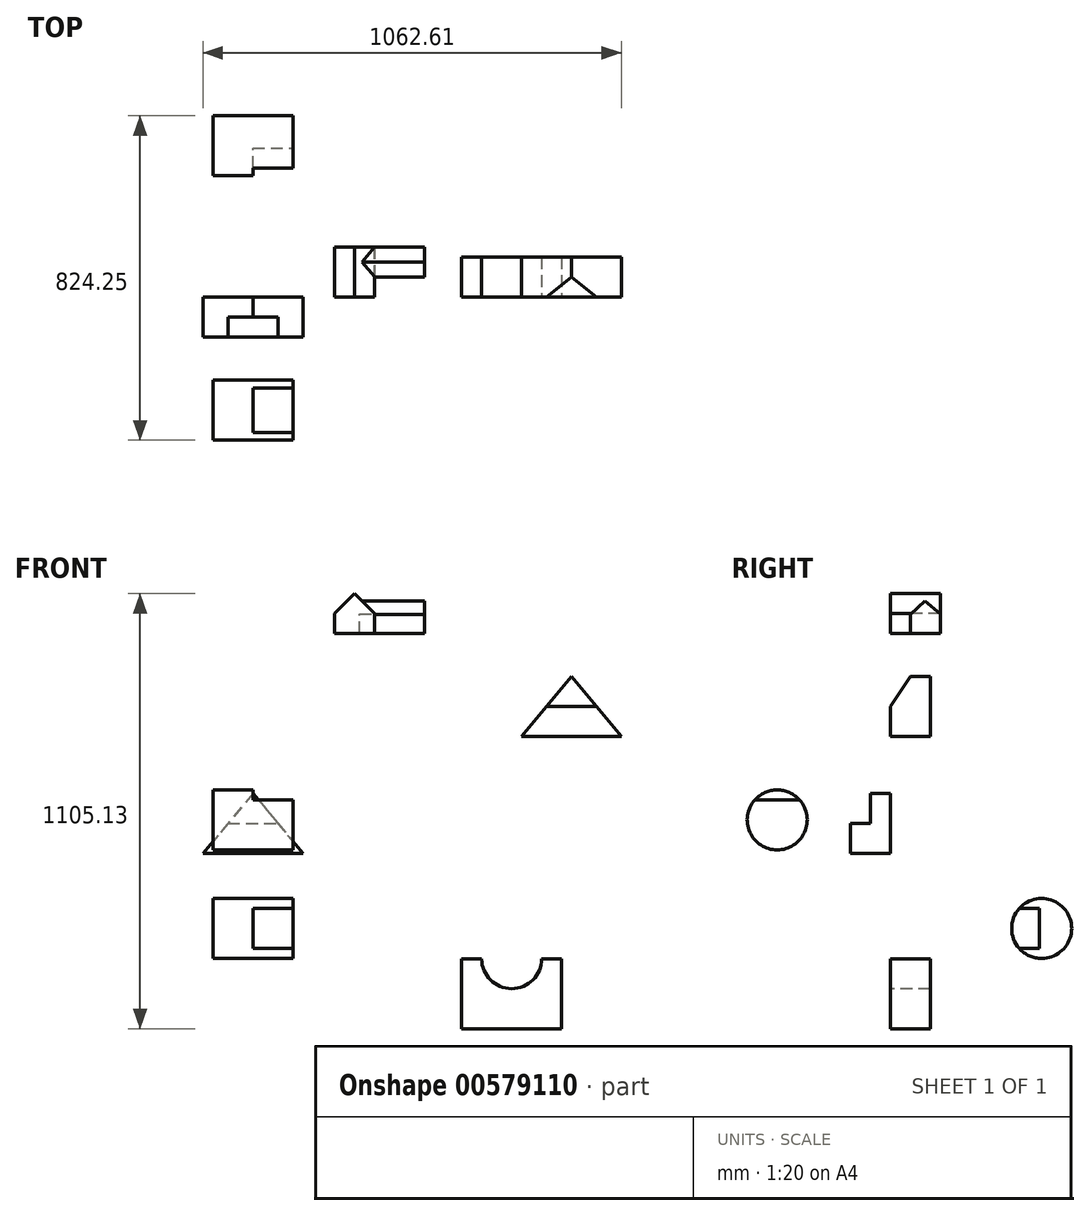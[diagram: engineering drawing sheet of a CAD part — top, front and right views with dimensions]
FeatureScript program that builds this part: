
annotation { "Feature Type Name" : "Feature", "Feature Type Description" : "" }
export const myFeature = defineFeature(function(context is Context, id is Id, definition is map)
    precondition{}
    {
        {
            var Q0;
            Q0=qCreatedBy(makeId("Front.planeOp"),FACE);
            var sketch = newSketch(context, id + "F0", { "sketchPlane" : qUnion([Q0])});
            skLineSegment(sketch, "E0", {"start": v(-228.36, -85.16) * mm, "end": v(25.64, -85.16) * mm});
            skLineSegment(sketch, "E1", {"start": v(-101.36, 67.24) * mm, "end": v(-37.86, -8.96) * mm});
            skLineSegment(sketch, "E2", {"start": v(-101.36, 67.24) * mm, "end": v(-164.86, -8.96) * mm});
            skLineSegment(sketch, "E3", {"start": v(-164.86, -8.96) * mm, "end": v(-37.86, -8.96) * mm});
            skLineSegment(sketch, "E4", {"start": v(-164.86, -8.96) * mm, "end": v(-228.36, -85.16) * mm});
            skLineSegment(sketch, "E5", {"start": v(-37.86, -8.96) * mm, "end": v(25.64, -85.16) * mm});
            skPoint(sketch, "E6.orphan", {"position": v(25.64, 67.24) * mm});
            skPoint(sketch, "E7.end.orphan", {"position": v(25.64, -8.96) * mm});
            skPoint(sketch, "E8.end.orphan", {"position": v(-228.36, -8.96) * mm});
            skPoint(sketch, "E9.end.orphan", {"position": v(-228.36, 67.24) * mm});
            skSolve(sketch);
        }
        {
            var Q0;
            Q0=makeQuery(id+"F0.imprint","IMPRINT",FACE,{"disambiguationData":[TD([[makeQuery(id+"F0.imprint","IMPRINT",EDGE,{"derivedFrom":sQuery(id+"F0.wireOp",EDGE,"E0")}),1.0]])]});
            extrude(context, id + "F1", {"entities" : qUnion([Q0]), "depth" : 101.6 * mm, "offsetDistance" : 25.4 * mm});
        }
        {
            var Q0;
            Q0 = qSketchRegion(id + "F0", true);
            extrude(context, id + "F2", {"entities" : qUnion([Q0]), "operationType" : NewBodyOperationType.ADD, "depth" : 50.8 * mm, "offsetDistance" : 25.4 * mm});
        }
        {
            var Q0;
            Q0=qCreatedBy(makeId("Front.planeOp"),FACE);
            var sketch = newSketch(context, id + "F3", { "sketchPlane" : qUnion([Q0])});
            skLineSegment(sketch, "E10", {"start": v(580.25, 364.98) * mm, "end": v(580.25, 212.58) * mm});
            skLineSegment(sketch, "E11", {"start": v(580.25, 212.58) * mm, "end": v(834.25, 212.58) * mm});
            skLineSegment(sketch, "E12", {"start": v(834.25, 212.58) * mm, "end": v(834.25, 364.98) * mm});
            skLineSegment(sketch, "E13", {"start": v(834.25, 364.98) * mm, "end": v(580.25, 364.98) * mm});
            skLineSegment(sketch, "E14", {"start": v(707.25, 364.98) * mm, "end": v(580.25, 212.58) * mm});
            skLineSegment(sketch, "E15", {"start": v(707.25, 364.98) * mm, "end": v(834.25, 212.58) * mm});
            skSolve(sketch);
        }
        {
            var Q0;
            Q0=makeQuery(id+"F3.imprint","IMPRINT",FACE,{"disambiguationData":[TD([[makeQuery(id+"F3.imprint","IMPRINT",EDGE,{"derivedFrom":sQuery(id+"F3.wireOp",EDGE,"E11")}),1.0]])]});
            extrude(context, id + "F4", {"entities" : qUnion([Q0]), "oppositeDirection" : true, "depth" : 101.6 * mm, "offsetDistance" : 25.4 * mm});
        }
        {
            var Q0;
            Q0=makeQuery(id+"F4.opExtrude","CAP_EDGE",EDGE,{"disambiguationData":[OSD([sQuery(id+"F3.wireOp",EDGE,"E11")])],"isStart":true});
            cPoint(context, id + "F5", {"entities" : qUnion([Q0]), "parameter" : 0.5});
        }
        {
            var Q0;
            Q0=makeQuery(id+"F4.opExtrude","CAP_VERTEX",VERTEX,{"disambiguationData":[OSD([sQuery(id+"F3.wireOp",EDGE,"E13"),sQuery(id+"F3.wireOp",EDGE,"E14"),sQuery(id+"F3.wireOp",EDGE,"E15")])],"isStart":true});
            var Q1;
            Q1=makeQuery(id+"F4.opExtrude","CAP_VERTEX",VERTEX,{"disambiguationData":[OSD([sQuery(id+"F3.wireOp",EDGE,"E13"),sQuery(id+"F3.wireOp",EDGE,"E14"),sQuery(id+"F3.wireOp",EDGE,"E15")])],"isStart":false});
            var Q2;
            Q2 = qCreatedBy(id + "F5" ,VERTEX);
            cPlane(context, id + "F6", {"entities" : qUnion([Q0, Q1, Q2]), "cplaneType" : CPlaneType.THREE_POINT, "offset" : 25.4 * mm, "width" : 152.4 * mm, "height" : 152.4 * mm});
        }
        {
            var Q0;
            Q0=qCreatedBy(id+"F6.planeOp",FACE);
            var sketch = newSketch(context, id + "F7", { "sketchPlane" : qUnion([Q0])});
            skLineSegment(sketch, "E16", {"start": v(0, 288.78) * mm, "end": v(50.8, 364.98) * mm});
            skLineSegment(sketch, "E17", {"start": v(50.8, 364.98) * mm, "end": v(0, 364.98) * mm});
            skLineSegment(sketch, "E18", {"start": v(0, 364.98) * mm, "end": v(0, 288.78) * mm});
            skSolve(sketch);
        }
        {
            var Q0;
            Q0 = qSketchRegion(id + "F7", true);
            extrude(context, id + "F8", {"entities" : qUnion([Q0]), "operationType" : NewBodyOperationType.REMOVE, "endBound" : BoundingType.SYMMETRIC, "oppositeDirection" : true, "depth" : 127 * mm, "offsetDistance" : 25.4 * mm});
        }
        {
            var Q0;
            Q0=qCreatedBy(makeId("Front.planeOp"),FACE);
            var sketch = newSketch(context, id + "F9", { "sketchPlane" : qUnion([Q0])});
            skLineSegment(sketch, "E19", {"start": v(106.32, 473.23) * mm, "end": v(207.92, 473.23) * mm});
            skLineSegment(sketch, "E20", {"start": v(207.92, 473.23) * mm, "end": v(207.92, 524.03) * mm});
            skLineSegment(sketch, "E21", {"start": v(207.92, 524.03) * mm, "end": v(157.12, 574.83) * mm});
            skPoint(sketch, "E21.endSnap0", {"position": v(157.12, 473.23) * mm});
            skLineSegment(sketch, "E22", {"start": v(106.32, 473.23) * mm, "end": v(106.32, 524.03) * mm});
            skLineSegment(sketch, "E23", {"start": v(106.32, 524.03) * mm, "end": v(157.12, 574.83) * mm});
            skLineSegment(sketch, "E24", {"start": v(207.92, 524.03) * mm, "end": v(334.92, 524.03) * mm});
            skLineSegment(sketch, "E25", {"start": v(334.92, 524.03) * mm, "end": v(334.92, 473.23) * mm});
            skLineSegment(sketch, "E26", {"start": v(334.92, 473.23) * mm, "end": v(207.92, 473.23) * mm});
            skSolve(sketch);
        }
        {
            var Q0;
            Q0=makeQuery(id+"F9.imprint","IMPRINT",FACE,{"disambiguationData":[TD([[makeQuery(id+"F9.imprint","IMPRINT",EDGE,{"derivedFrom":sQuery(id+"F9.wireOp",EDGE,"E19")}),1.0]])]});
            extrude(context, id + "F10", {"entities" : qUnion([Q0]), "oppositeDirection" : true, "depth" : 127 * mm, "offsetDistance" : 25.4 * mm});
        }
        {
            var Q0;
            Q0=makeQuery(id+"F10.opExtrude","SWEPT_FACE",FACE,{"disambiguationData":[OSD([sQuery(id+"F9.wireOp",EDGE,"E20")])]});
            cPlane(context, id + "F11", {"entities" : qUnion([Q0]), "cplaneType" : CPlaneType.OFFSET, "offset" : 127 * mm, "width" : 152.4 * mm, "height" : 152.4 * mm});
        }
        {
            var Q0;
            Q0=qCreatedBy(id+"F11.planeOp",FACE);
            var sketch = newSketch(context, id + "F12", { "sketchPlane" : qUnion([Q0])});
            skLineSegment(sketch, "E27", {"start": v(50.27, 473.7) * mm, "end": v(50.27, 522.32) * mm});
            skLineSegment(sketch, "E28", {"start": v(50.27, 522.32) * mm, "end": v(88.37, 555.92) * mm});
            skPoint(sketch, "E28.endSnap0", {"position": v(88.37, 473.7) * mm});
            skLineSegment(sketch, "E29", {"start": v(88.37, 555.92) * mm, "end": v(127.37, 523.36) * mm});
            skLineSegment(sketch, "E30", {"start": v(50.27, 473.7) * mm, "end": v(127.09, 473.7) * mm});
            skLineSegment(sketch, "E31", {"start": v(127.09, 473.7) * mm, "end": v(127.37, 523.36) * mm});
            skSolve(sketch);
        }
        {
            var Q0;
            Q0 = qSketchRegion(id + "F12", true);
            extrude(context, id + "F13", {"entities" : qUnion([Q0]), "operationType" : NewBodyOperationType.ADD, "oppositeDirection" : true, "depth" : 165.1 * mm, "offsetDistance" : 25.4 * mm});
        }
        {
            var Q0;
            Q0=qCreatedBy(makeId("Right.planeOp"),FACE);
            var sketch = newSketch(context, id + "F14", { "sketchPlane" : qUnion([Q0])});
            skCircle(sketch, "E32", {"center": v(-287.54, 0) * mm, "radius": 76.2 * mm});
            skSolve(sketch);
        }
        {
            var Q0;
            Q0=makeQuery(id+"F14.imprint","IMPRINT",FACE,{"disambiguationData":[TD([[makeQuery(id+"F14.imprint","IMPRINT",EDGE,{"derivedFrom":sQuery(id+"F14.wireOp",EDGE,"E32")}),1.0]])]});
            extrude(context, id + "F15", {"entities" : qUnion([Q0]), "oppositeDirection" : true, "depth" : 203.2 * mm, "offsetDistance" : 25.4 * mm});
        }
        {
            var Q0;
            Q0=makeQuery(id+"F15.opExtrude","CAP_FACE",FACE,{"disambiguationData":[OSD([sQuery(id+"F14.wireOp",EDGE,"E32")])],"isStart":true});
            var sketch = newSketch(context, id + "F16", { "sketchPlane" : qUnion([Q0])});
            skLineSegment(sketch, "E33", {"start": v(-344.34, 50.8) * mm, "end": v(-230.75, 50.8) * mm});
            skSolve(sketch);
        }
        {
            var Q0;
            {var subQ0=sQuery(id+"F16.wireOp",EDGE,"E33");Q0=makeQuery(id+"F16.imprint","IMPRINT",FACE,{"disambiguationData":[TD([[makeQuery(id+"F16.imprint","IMPRINT",EDGE,{"derivedFrom":subQ0}),1.0]])]});}
            extrude(context, id + "F17", {"entities" : qUnion([Q0]), "operationType" : NewBodyOperationType.REMOVE, "oppositeDirection" : true, "depth" : 101.6 * mm, "offsetDistance" : 25.4 * mm});
        }
        {
            var Q0;
            Q0=qCreatedBy(makeId("Right.planeOp"),FACE);
            var sketch = newSketch(context, id + "F18", { "sketchPlane" : qUnion([Q0])});
            skCircle(sketch, "E34", {"center": v(384.31, -275.82) * mm, "radius": 76.2 * mm});
            skSolve(sketch);
        }
        {
            var Q0;
            Q0 = qSketchRegion(id + "F18", true);
            extrude(context, id + "F19", {"entities" : qUnion([Q0]), "oppositeDirection" : true, "depth" : 203.2 * mm, "offsetDistance" : 25.4 * mm});
        }
        {
            var Q0;
            Q0=makeQuery(id+"F19.opExtrude","CAP_FACE",FACE,{"disambiguationData":[OSD([sQuery(id+"F18.wireOp",EDGE,"E34")])],"isStart":true});
            var sketch = newSketch(context, id + "F20", { "sketchPlane" : qUnion([Q0])});
            skLineSegment(sketch, "E35", {"start": v(327.52, -225.02) * mm, "end": v(378.32, -225.02) * mm});
            skLineSegment(sketch, "E36", {"start": v(378.32, -225.02) * mm, "end": v(378.32, -326.62) * mm});
            skLineSegment(sketch, "E37", {"start": v(378.32, -326.62) * mm, "end": v(327.52, -326.62) * mm});
            skSolve(sketch);
        }
        {
            var Q0;
            {var subQ0=sQuery(id+"F20.wireOp",EDGE,"E35");Q0=makeQuery(id+"F20.imprint","IMPRINT",FACE,{"disambiguationData":[TD([[makeQuery(id+"F20.imprint","IMPRINT",EDGE,{"derivedFrom":subQ0}),-1.0]])]});}
            extrude(context, id + "F21", {"entities" : qUnion([Q0]), "operationType" : NewBodyOperationType.REMOVE, "oppositeDirection" : true, "depth" : 101.6 * mm, "offsetDistance" : 25.4 * mm});
        }
        {
            var Q0;
            Q0=qCreatedBy(makeId("Front.planeOp"),FACE);
            var sketch = newSketch(context, id + "F22", { "sketchPlane" : qUnion([Q0])});
            skLineSegment(sketch, "E38", {"start": v(428.81, -352.5) * mm, "end": v(428.81, -530.3) * mm});
            skLineSegment(sketch, "E39", {"start": v(428.81, -530.3) * mm, "end": v(682.81, -530.3) * mm});
            skLineSegment(sketch, "E40", {"start": v(682.81, -530.3) * mm, "end": v(682.81, -352.5) * mm});
            skLineSegment(sketch, "E41", {"start": v(682.81, -352.5) * mm, "end": v(428.81, -352.5) * mm});
            skCircle(sketch, "E42", {"center": v(555.81, -352.5) * mm, "radius": 76.2 * mm});
            skSolve(sketch);
        }
        {
            var Q0;
            {var subQ4=sQuery(id+"F22.wireOp",EDGE,"E38");Q0=makeQuery(id+"F22.imprint","IMPRINT",FACE,{"disambiguationData":[TD([[makeQuery(id+"F22.imprint","IMPRINT",EDGE,{"derivedFrom":subQ4}),1.0]])]});}
            var Q1;
            {var subQ0=sQuery(id+"F22.wireOp",EDGE,"E42");var subQ1=sQuery(id+"F22.wireOp",EDGE,"E41");var subQ2=makeQuery(id+"F22.imprint","INTERSECT",VERTEX,{"disambiguationData":[OD(0.0)],"derivedFrom":[subQ1,subQ0]});Q1=makeQuery(id+"F22.imprint","IMPRINT",FACE,{"disambiguationData":[TD([[makeQuery(id+"F22.imprint","IMPRINT",EDGE,{"disambiguationData":[TD([[subQ2,-1.0]])],"derivedFrom":subQ1}),1.0]])]});}
            extrude(context, id + "F23", {"entities" : qUnion([Q0, Q1]), "oppositeDirection" : true, "depth" : 101.6 * mm, "offsetDistance" : 25.4 * mm});
        }
        {
            var Q0;
            Q0=makeQuery(id+"F23.opExtrude","CAP_FACE",FACE,{"disambiguationData":[OSD([sQuery(id+"F22.wireOp",EDGE,"E38"),sQuery(id+"F22.wireOp",EDGE,"E39"),sQuery(id+"F22.wireOp",EDGE,"E40"),sQuery(id+"F22.wireOp",EDGE,"E41")])],"isStart":true});
            var sketch = newSketch(context, id + "F24", { "sketchPlane" : qUnion([Q0])});
            skCircle(sketch, "E43", {"center": v(556.23, -353.25) * mm, "radius": 76.2 * mm});
            skPoint(sketch, "E43.first.point", {"position": v(480.03, -352.5) * mm});
            skPoint(sketch, "E43.second.point", {"position": v(615.78, -400.78) * mm});
            skPoint(sketch, "E43.third.point", {"position": v(632.42, -352.5) * mm});
            skSolve(sketch);
        }
        {
            var Q0;
            {var subQ0=sQuery(id+"F24.wireOp",EDGE,"E43");var subQ1=makeQuery(id+"F23.opExtrude","CAP_EDGE",EDGE,{"disambiguationData":[OSD([sQuery(id+"F22.wireOp",EDGE,"E41")])],"isStart":true});var subQ2=makeQuery(id+"F24.imprint","INTERSECT",VERTEX,{"disambiguationData":[OD(0.0)],"derivedFrom":[subQ1,subQ0]});Q0=makeQuery(id+"F24.imprint","IMPRINT",FACE,{"disambiguationData":[TD([[makeQuery(id+"F24.imprint","IMPRINT",EDGE,{"disambiguationData":[TD([[subQ2,-1.0]])],"derivedFrom":subQ0}),1.0]])]});}
            extrude(context, id + "F25", {"entities" : qUnion([Q0]), "operationType" : NewBodyOperationType.REMOVE, "oppositeDirection" : true, "depth" : 50.8 * mm, "offsetDistance" : 25.4 * mm});
        }
    });
